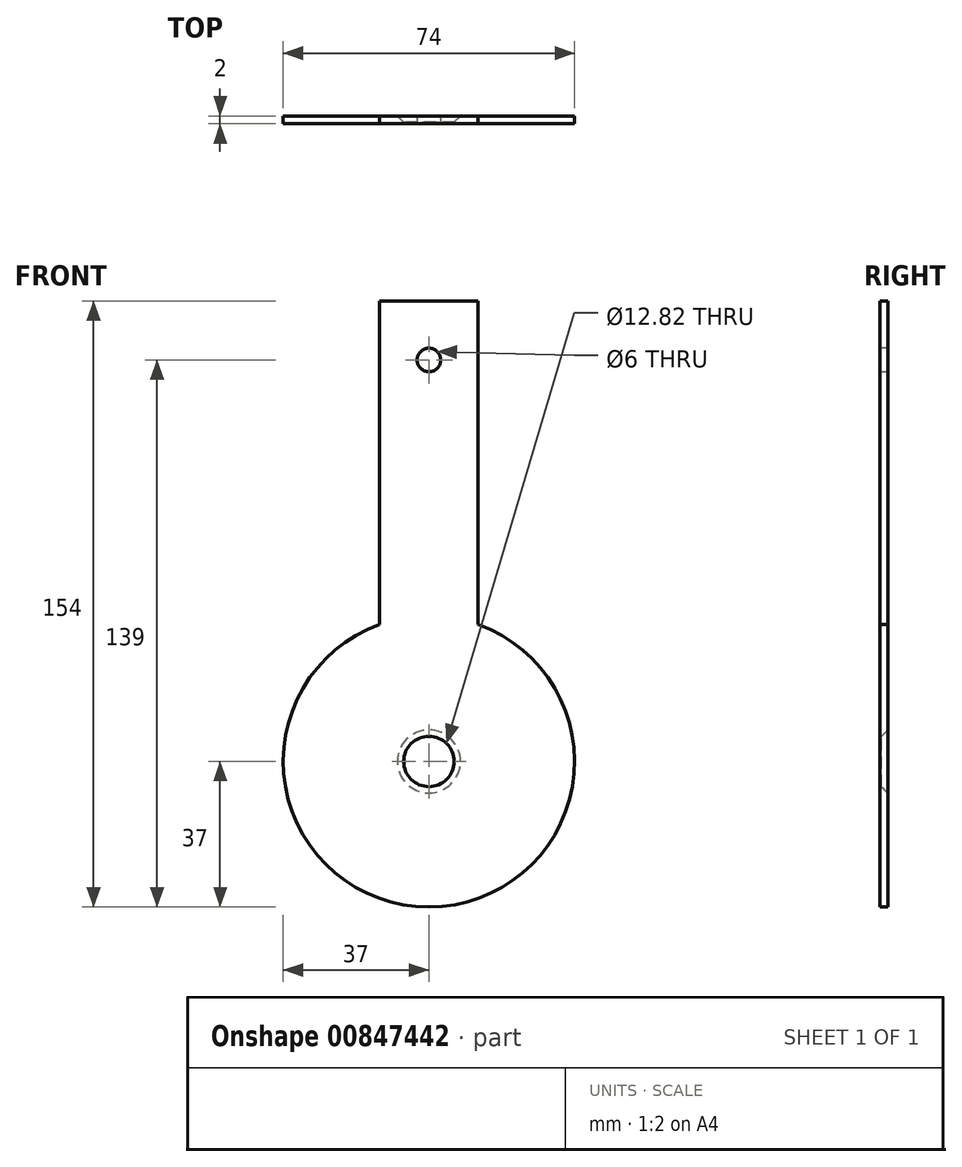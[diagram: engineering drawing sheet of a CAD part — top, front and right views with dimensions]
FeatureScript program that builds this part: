
annotation { "Feature Type Name" : "Feature", "Feature Type Description" : "" }
export const myFeature = defineFeature(function(context is Context, id is Id, definition is map)
    precondition{}
    {
        {
            var Q0;
            Q0=qCreatedBy(makeId("Front.planeOp"),FACE);
            var sketch = newSketch(context, id + "F0", { "sketchPlane" : qUnion([Q0])});
            skLineSegment(sketch, "E0", {"start": v(0, 69.74) * mm, "end": v(0, -68.9) * mm, "construction": true});
            skLineSegment(sketch, "E1", {"start": v(-63.43, 0) * mm, "end": v(67.98, 0) * mm, "construction": true});
            skCircle(sketch, "E2", {"center": v(0, 0) * mm, "radius": 37 * mm});
            skCircle(sketch, "E3", {"center": v(0, 0) * mm, "radius": 6.4 * mm});
            skSolve(sketch);
        }
        {
            var Q0;
            Q0 = qSketchRegion(id + "F0", true);
            extrude(context, id + "F1", {"entities" : qUnion([Q0]), "oppositeDirection" : true, "depth" : 2 * mm, "offsetDistance" : 25 * mm});
        }
        {
            var Q0;
            Q0=makeQuery(id+"F1.opExtrude","CAP_FACE",FACE,{"disambiguationData":[OSD([sQuery(id+"F0.wireOp",EDGE,"E2"),sQuery(id+"F0.wireOp",EDGE,"E3")])],"isStart":true});
            var sketch = newSketch(context, id + "F2", { "sketchPlane" : qUnion([Q0])});
            skLineSegment(sketch, "E4", {"start": v(0, 132.36) * mm, "end": v(0, -45.23) * mm, "construction": true});
            skLineSegment(sketch, "E5", {"start": v(-50.22, 37) * mm, "end": v(46.1, 37) * mm, "construction": true});
            skLineSegment(sketch, "E6.bottom", {"start": v(-12.5, 117) * mm, "end": v(12.5, 117) * mm});
            skLineSegment(sketch, "E6.left", {"start": v(-12.5, 117) * mm, "end": v(-12.5, 34.82) * mm});
            skLineSegment(sketch, "E6.right", {"start": v(12.5, 117) * mm, "end": v(12.5, 34.82) * mm});
            skArc(sketch, "E7.0", {"start": v(12.5, 34.82) * mm, "mid": v(0, 37) * mm, "end": v(-12.5, 34.82) * mm});
            skSolve(sketch);
        }
        {
            var Q0;
            Q0 = qSketchRegion(id + "F2", true);
            extrude(context, id + "F3", {"entities" : qUnion([Q0]), "operationType" : NewBodyOperationType.ADD, "oppositeDirection" : true, "depth" : 2 * mm, "offsetDistance" : 25 * mm});
        }
        {
            var Q0;
            Q0=makeQuery(id+"F3.boolean.opBoolean","MERGE",FACE,{"derivedFrom":[makeQuery(id+"F1.opExtrude","CAP_FACE",FACE,{"disambiguationData":[OSD([sQuery(id+"F0.wireOp",EDGE,"E2"),sQuery(id+"F0.wireOp",EDGE,"E3")])],"isStart":true}),makeQuery(id+"F3.opExtrude","CAP_FACE",FACE,{"disambiguationData":[OSD([sQuery(id+"F2.wireOp",EDGE,"E6.bottom"),sQuery(id+"F2.wireOp",EDGE,"E6.left"),sQuery(id+"F2.wireOp",EDGE,"E6.right"),sQuery(id+"F2.wireOp",EDGE,"E7.0")])],"isStart":true})]});
            var sketch = newSketch(context, id + "F4", { "sketchPlane" : qUnion([Q0])});
            skLineSegment(sketch, "E8.0", {"start": v(-12.5, 117) * mm, "end": v(12.5, 117) * mm, "construction": true});
            skLineSegment(sketch, "E9", {"start": v(-39.3, 102) * mm, "end": v(47.9, 102) * mm, "construction": true});
            skLineSegment(sketch, "E10", {"start": v(0, 127.5) * mm, "end": v(0, -52.45) * mm, "construction": true});
            skCircle(sketch, "E11", {"center": v(0, 102) * mm, "radius": 3 * mm});
            skSolve(sketch);
        }
        {
            var Q0;
            Q0 = qSketchRegion(id + "F4", true);
            extrude(context, id + "F5", {"entities" : qUnion([Q0]), "operationType" : NewBodyOperationType.REMOVE, "endBound" : BoundingType.THROUGH_ALL, "oppositeDirection" : true, "depth" : 25 * mm, "offsetDistance" : 25 * mm});
        }
        {
            var Q0;
            Q0=makeQuery(id+"F1.opExtrude","CAP_EDGE",EDGE,{"disambiguationData":[OSD([sQuery(id+"F0.wireOp",EDGE,"E3")])],"isStart":false});
            chamfer(context, id + "F6", {"entities" : qUnion([Q0]), "chamferType" : ChamferType.OFFSET_ANGLE, "width" : 1.6 * mm, "oppositeDirection" : false, "angle" : 45 * degree, "tangentPropagation" : true});
        }
    });
